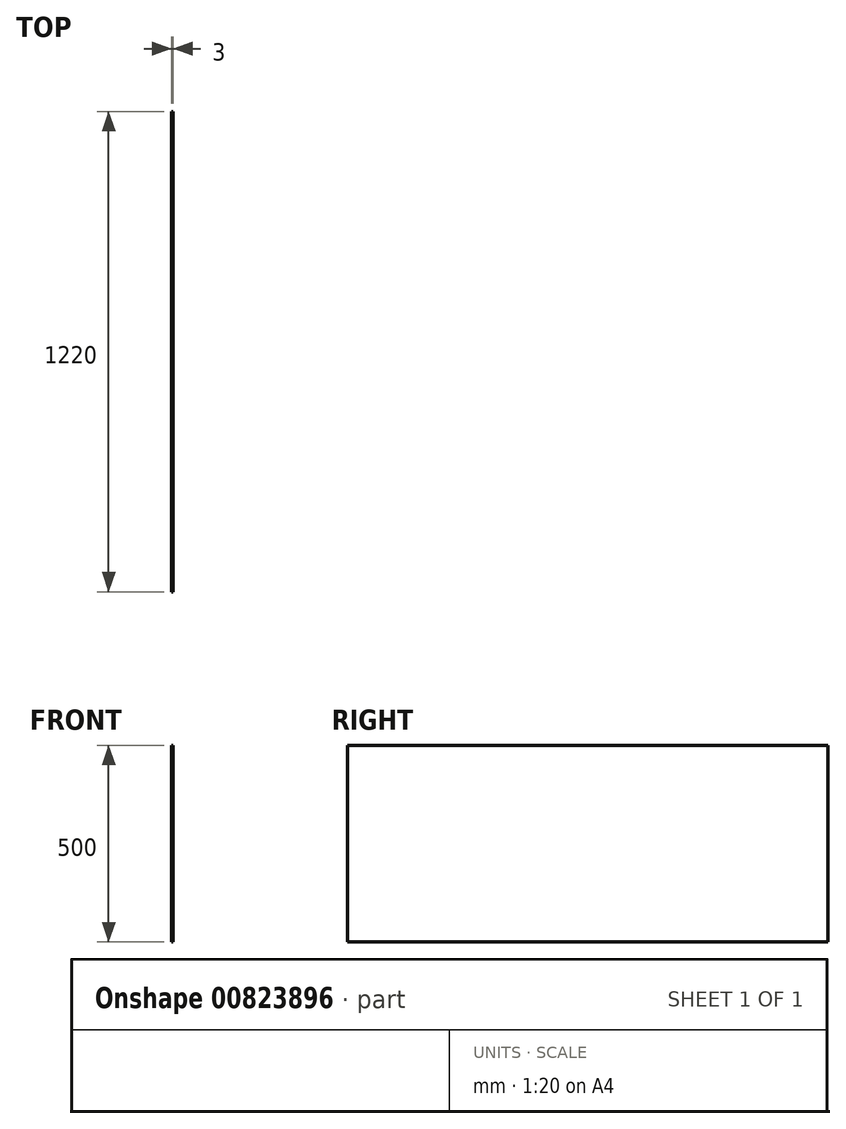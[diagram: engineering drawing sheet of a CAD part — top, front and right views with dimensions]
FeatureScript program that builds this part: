
annotation { "Feature Type Name" : "Feature", "Feature Type Description" : "" }
export const myFeature = defineFeature(function(context is Context, id is Id, definition is map)
    precondition{}
    {
        {
            var Q0;
            Q0=qCreatedBy(makeId("Right.planeOp"),FACE);
            var sketch = newSketch(context, id + "F0", { "sketchPlane" : qUnion([Q0])});
            skLineSegment(sketch, "E0.bottom", {"start": v(-610, 250) * mm, "end": v(610, 250) * mm});
            skLineSegment(sketch, "E0.top", {"start": v(-610, -250) * mm, "end": v(610, -250) * mm});
            skLineSegment(sketch, "E0.left", {"start": v(-610, 250) * mm, "end": v(-610, -250) * mm});
            skLineSegment(sketch, "E0.right", {"start": v(610, 250) * mm, "end": v(610, -250) * mm});
            skPoint(sketch, "E0.middle", {"position": v(0, 0) * mm});
            skSolve(sketch);
        }
        {
            var Q0;
            Q0=makeQuery(id+"F0.imprint","IMPRINT",FACE,{"disambiguationData":[TD([[makeQuery(id+"F0.imprint","IMPRINT",EDGE,{"derivedFrom":sQuery(id+"F0.wireOp",EDGE,"E0.bottom")}),-1.0]])]});
            extrude(context, id + "F1", {"entities" : qUnion([Q0]), "depth" : 3 * mm, "offsetDistance" : 25 * mm});
        }
    });
